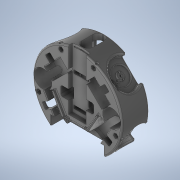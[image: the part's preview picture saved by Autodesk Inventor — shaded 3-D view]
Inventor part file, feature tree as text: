
AUTODESK INVENTOR PART (.ipt)
format: ipt  version: 2020.4 (Build 244396000, 396)  size: 3,471,872 bytes
history: native  units: mm
features: extrude x76, sketch x74, projected_geometry x35, fillet x19, other x9, chamfer x4, plane x2, mirror x1
ambient origin geometry x8: Origin, YZ Plane, XZ Plane, XY Plane, X Axis, Y Axis, Z Axis, Center Point
bodies: Solid1 (feature_tree)
feature tree (220):
  extrude  "Cilinder"  Depth=54.0mm TaperAngle=0.0deg
  other  "Motor Axis"
  other  "Plano M1"
  other  "Plano M2"
  other  "Plano M3"
  other  "Plano M4"
  extrude  "Roda M1"  Depth=176.0mm
  extrude  "Roda M2"  TaperAngle=60.0deg  [1 undecoded]
  extrude  "Roda M3"  TaperAngle=45.0deg  [1 undecoded]
  extrude  "Roda M4"  TaperAngle=0.0deg  [1 undecoded]
  extrude  "MotorsFitting"  Depth=14.6mm TaperAngle=0.0deg
  fillet  "MotorsCurve"  Radius=55.0mm
  extrude  "Threads M1"  Depth=20.0mm
  extrude  "Threads M2"  Depth=55.0mm
  extrude  "Threads M3"  Depth=20.0mm
  extrude  "Threads M4"  Depth=55.0mm
  extrude  "Threads Head M1"  Depth=20.0mm
  extrude  "Threads Head M2"  Depth=9.4mm
  extrude  "Threads Head M3"  Depth=9.4mm
  extrude  "Threads Head M4"  Depth=23.0mm
  extrude  "Thread Depth M1"  Depth=9.4mm
  extrude  "Thread Depth M2"  Depth=45.0mm
  extrude  "Thread Depth M3"  Depth=45.0mm
  extrude  "Thread Depth M4"  Depth=30.0mm
  extrude  "Threads Nut Head M1"  Depth=32.5mm
  extrude  "Threads Nut Head M2"  Depth=40.0mm TaperAngle=0.0deg
  extrude  "Threads Nut Head M3"  Depth=5.0mm
  extrude  "Threads Nut Head M4"  TaperAngle=0.0deg  [1 undecoded]
  extrude  "Wheel Fitting M1"  Depth=3.0mm
  extrude  "Wheel Fitting M2"  TaperAngle=0.0deg  [1 undecoded]
  extrude  "Wheel Fitting M3"  Depth=30.0mm TaperAngle=360.0deg
  extrude  "Wheel Fitting M4"  Depth=2.0mm
  extrude  "Capacitors"  Depth=6.0mm
  extrude  "Gear Entrance M1"  Depth=19.5mm
  extrude  "Gear Entrance M2"  Depth=10.0mm
  extrude  "Gear Entrance M3"  Depth=2.0mm
  extrude  "Gear Entrance M4"  Depth=2.0mm
  fillet  "Rounding Edges"  Radius=3.0mm
  fillet  "Rounding Motor Entrances"  Radius=6.0mm
  extrude  "Standoff Fitting"  TaperAngle=0.0deg  [1 undecoded]
  extrude  "Standoff Thread M1"  Depth=19.6mm
  extrude  "Standoff Thread M2"  Depth=19.5mm
  extrude  "Standoff Thread M3"  TaperAngle=0.0deg  [1 undecoded]
  extrude  "Standoff Thread M4"  Depth=30.0mm TaperAngle=360.0deg
  other  "Standoff Plane M1"
  other  "Standoff Plane M2"
  other  "Standoff Plane M3"
  other  "Standoff Plane M4"
  extrude  "Standoff Head M1"  Depth=10.0mm
  extrude  "Standoff Head M2"  Depth=2.0mm
  extrude  "Standoff Head M3"  TaperAngle=0.0deg  [1 undecoded]
  extrude  "Standoff Head M4"  Depth=6.0mm
  extrude  "Dribbler Entrance"  Depth=19.5mm
  extrude  "Battery Fitting"  Depth=19.6mm
  fillet  "Motor to Battery Edges"  Radius=3.0mm
  extrude  "Front Kicker"  Depth=11.0mm
  fillet  "Front Edges"  Radius=30.0mm
  extrude  "Cover Inlet"  Depth=10.0mm TaperAngle=0.0deg
  extrude  "Capacitors Holes"  Depth=2.0mm
  extrude  "Dribbler Motor Space"  Depth=2.0mm
  extrude  "IR Holder"  TaperAngle=0.0deg  [1 undecoded]
  fillet  "Dribbler and Kicker Edges"  Radius=19.5mm
  fillet  "Minor Fixes"  Radius=19.5mm
  chamfer  "Dribbler Chanfer"  Distance=30.0mm Angle=360.0deg
  extrude  "Capacitor Cable Fittng 1"  Depth=10.0mm TaperAngle=0.0deg
  fillet  "Capacitor Cable Rounding"  Radius=5.5mm
  extrude  "Special Nut M1"  Depth=5.5mm
  extrude  "Special Nut M2"  Depth=5.5mm
  extrude  "Special Nut M3"  Depth=5.5mm
  extrude  "Special Nut M4"  Depth=5.5mm
  extrude  "Special Nut Cylinder M1"  Depth=5.5mm
  extrude  "Special Nut Cylinder M2"  Depth=5.5mm
  extrude  "Special Nut Cylinder M3"  Depth=5.5mm
  extrude  "Special Nut Cylinder M4"  Depth=4.0mm
  fillet  "Special Nut Rounding"  Radius=4.0mm
  extrude  "Kicker Plate Fit 1"  Depth=4.0mm
  extrude  "Kicker Front Opening"  Depth=17.75mm TaperAngle=0.0deg
  extrude  "Kicker Base Fit"  Depth=4.0mm
  extrude  "Coil and Plinge Fitting"  Depth=4.0mm
  extrude  "Kicker Pkate Plunge Fit"  Depth=17.75mm TaperAngle=0.0deg
  chamfer  "Plunge Entrance 1"  Distance=17.6mm
  chamfer  "Plunge Entrance 2"  Distance=17.6mm
  fillet  "Fillet11"  Radius=15.5mm
  chamfer  "Coil Edges 1"  Distance=17.6mm
  extrude  "Kicker Plate Threads"  Depth=32.0mm
  extrude  "kicker Plate Nut 1"  Depth=2.0mm
  extrude  "Kicker Plate Nut 2"  Depth=2.0mm
  extrude  "Kicker Plunge Fit"  Depth=2.0mm
  fillet  "Kicker Plunge Round"  Radius=68.0mm
  fillet  "Wheel Round"  Radius=50.0mm
  extrude  "Capacitor Cables"  Depth=2.0mm
  fillet  "Capacitor Cable Round 1"  Radius=14.0mm
  fillet  "Capacitor Cable Round 2"  Radius=10.0mm
  extrude  "MotorProtection"  Depth=2.0mm
  fillet  "Motor Protection Round"  Radius=10.0mm
  extrude  "Extrusion86"  Depth=2.0mm TaperAngle=0.0deg
  extrude  "Extrusion87"  Depth=2.0mm
  fillet  "Fillet17"  Radius=10.0mm
  extrude  "Extrusion88"  Depth=2.0mm TaperAngle=0.0deg
  plane  "Work Plane14"
  extrude  "Extrusion89"  Depth=2.0mm
  extrude  "Extrusion91"  Depth=10.0mm
  mirror  "Mirror3"
  fillet  "Fillet18"  Radius=14.0mm
  extrude  "Extrusion92"  Depth=2.0mm
  fillet  "Fillet19"  Radius=2.0mm
  extrude  "Extrusion93"  Depth=2.0mm
  fillet  "Fillet20"  Radius=22.0mm
  extrude  "Extrusion94"  Depth=2.0mm
  extrude  "Extrusion95"  Depth=2.0mm
  sketch  "Sketch1"  dims[d0=176.0mm d1=54.0mm d2=0.0mm]
  sketch  "Sketch3"  dims[d3=180.0mm d4=176.0mm]
  sketch  "Sketch4"  dims[d5=60.0deg d6=60.0deg]
  sketch  "Sketch5"  dims[d8=45.0deg d9=45.0deg]
  sketch  "Sketch6"  dims[d10=55.0mm d11=0.0mm]
  sketch  "Sketch7"  dims[d12=20.0mm d13=14.6mm d14=0.0mm d15=55.0mm]
  sketch  "Sketch8"  dims[d16=0.0mm d17=20.0mm]
  sketch  "Sketch9"  dims[d18=14.6mm d19=0.0mm d20=55.0mm]
  sketch  "Sketch10"  dims[d21=0.0mm d22=20.0mm]
  sketch  "Sketch11"  dims[d23=14.6mm d24=0.0mm d25=55.0mm]
  sketch  "Sketch12"  dims[d26=0.0mm d27=20.0mm]
  sketch  "Sketch13"  dims[d28=14.6mm d29=0.0mm d30=9.4mm]
  sketch  "Sketch14"  dims[d32=9.4mm d33=9.4mm]
  sketch  "Sketch15"  dims[d34=23.0mm d35=23.0mm]
  sketch  "Sketch16"  dims[d37=23.0mm d38=9.4mm]
  sketch  "Sketch17"  dims[d39=23.0mm d40=45.0mm]
  sketch  "Sketch18"  dims[d41=45.0mm d42=45.0mm]
  sketch  "Sketch19"  dims[d43=45.0mm d44=30.0mm]
  sketch  "Sketch20"  dims[d45=30.0mm d46=32.5mm]
  sketch  "Sketch21"  dims[d47=32.5mm d48=40.0mm d49=0.0mm]
  sketch  "Sketch22"  dims[d50=22.5mm d51=5.0mm]
  sketch  "Sketch23"  dims[d52=12.5mm d53=0.0mm]
  sketch  "Sketch24"  dims[d54=19.5mm d55=3.0mm]
  sketch  "Sketch25"  dims[d56=19.6mm d58=0.0mm]
  sketch  "Sketch26"  dims[d59=11.0mm d60=30.0mm d62=360.0deg]
  sketch  "Sketch27"  dims[d64=2.0mm d65=2.0mm]
  sketch  "Sketch28"  dims[d66=6.0mm d67=6.0mm]
  sketch  "Sketch29"  dims[d68=19.5mm d69=19.5mm]
  sketch  "Sketch30"  dims[d70=10.0mm d71=0.0mm d72=2.5mm]
  projected_geometry  "Projected Loop1"
  sketch  "Sketch31"  dims[d73=5.0mm d74=2.0mm]
  projected_geometry  "Projected Loop2"
  sketch  "Sketch32"  dims[d75=2.0mm d76=12.5mm d77=3.0mm d78=6.0mm]
  projected_geometry  "Projected Loop3"
  sketch  "Sketch33"  dims[d79=6.0mm d80=0.0mm]
  projected_geometry  "Projected Loop4"
  sketch  "Sketch34"  dims[d81=19.5mm d82=19.6mm]
  sketch  "Sketch35"  dims[d83=19.5mm d84=19.5mm]
  projected_geometry  "Projected Loop5"
  sketch  "Sketch36"  dims[d85=5.0mm d86=0.0mm]
  projected_geometry  "Projected Loop6"
  sketch  "Sketch37"  dims[d87=11.0mm d88=30.0mm d90=360.0deg]
  projected_geometry  "Projected Loop7"
  sketch  "Sketch38"  dims[d92=10.0mm d93=0.0mm d94=5.0mm]
  projected_geometry  "Projected Loop8"
  sketch  "Sketch39"  dims[d95=12.5mm d96=2.0mm]
  sketch  "Sketch40"  dims[d97=2.0mm d98=0.0mm]
  sketch  "Sketch41"  dims[d99=19.5mm d100=6.0mm]
  sketch  "Sketch42"  dims[d101=6.0mm d102=19.5mm]
  sketch  "Sketch43"  dims[d103=19.5mm d104=19.6mm d105=3.0mm]
  sketch  "Sketch44"  dims[d106=0.0mm d107=11.0mm d108=30.0mm d110=360.0deg]
  projected_geometry  "Projected Loop9"
  projected_geometry  "Projected Loop10"
  sketch  "Sketch45"  dims[d112=5.0mm d113=10.0mm d114=0.0mm]
  sketch  "Sketch46"  dims[d115=5.0mm d116=2.0mm]
  projected_geometry  "Projected Loop11"
  projected_geometry  "Projected Loop12"
  sketch  "Sketch48"  dims[d117=2.0mm d118=6.0mm]
  projected_geometry  "Projected Loop14"
  sketch  "Sketch50"  dims[d119=6.0mm d120=0.0mm d121=19.5mm d122=19.5mm]
  projected_geometry  "Projected Loop15"
  sketch  "Sketch59"  dims[d123=19.5mm]
  sketch  "Sketch64"  dims[d124=12.5mm]
  sketch  "Sketch65"  dims[d125=19.6mm]
  projected_geometry  "Projected Loop27"
  sketch  "Sketch66"  dims[d126=3.0mm]
  projected_geometry  "Projected Loop28"
  sketch  "Sketch67"  dims[d127=0.0mm]
  sketch  "Sketch68"  dims[d128=11.0mm d129=30.0mm d131=360.0deg]
  sketch  "Sketch69"  dims[d133=2.5mm d134=10.0mm d135=0.0mm d136=5.5mm]
  sketch  "Sketch70"  dims[d137=5.5mm d138=5.5mm]
  sketch  "Sketch71"  dims[d139=18.0mm d140=0.0mm d141=5.5mm]
  sketch  "Sketch72"  dims[d142=5.5mm d143=5.5mm]
  projected_geometry  "Projected Loop29"
  sketch  "Sketch73"  dims[d144=18.0mm d145=0.0mm d146=5.5mm]
  sketch  "Sketch74"  dims[d147=5.5mm d148=5.5mm]
  projected_geometry  "Projected Loop30"
  sketch  "Sketch75"  dims[d149=18.0mm d150=0.0mm d151=5.5mm]
  projected_geometry  "Projected Loop31"
  sketch  "Sketch76"  dims[d152=5.5mm d153=5.5mm]
  projected_geometry  "Projected Loop32"
  projected_geometry  "Projected Loop33"
  sketch  "Sketch77"  dims[d154=18.0mm d155=0.0mm d156=4.0mm d157=4.0mm]
  projected_geometry  "Projected Loop34"
  projected_geometry  "Projected Loop35"
  projected_geometry  "Projected Loop36"
  projected_geometry  "Projected Loop37"
  sketch  "Sketch78"  dims[d158=17.75mm d159=0.0mm d160=4.0mm]
  sketch  "Sketch80"  dims[d161=4.0mm d162=17.75mm d163=0.0mm]
  projected_geometry  "Projected Loop38"
  projected_geometry  "Projected Loop39"
  projected_geometry  "Projected Loop40"
  projected_geometry  "Projected Loop41"
  sketch  "Sketch81"  dims[d164=4.0mm d165=4.0mm]
  sketch  "Sketch82"  dims[d166=17.75mm d167=0.0mm d168=4.0mm]
  sketch  "Sketch89"  dims[d169=4.0mm d170=17.75mm d171=0.0mm]
  sketch  "Sketch90"  dims[d172=15.5mm]
  sketch  "Sketch92"  dims[d173=32.0mm d174=17.6mm d175=0.0mm]
  sketch  "Sketch93"  dims[d176=15.5mm]
  sketch  "Sketch95"  dims[d177=32.0mm d178=17.6mm d179=0.0mm d180=15.5mm]
  plane  "Work Plane15"
  projected_geometry  "Projected Loop46"
  projected_geometry  "Projected Loop47"
  projected_geometry  "Projected Loop48"
  sketch  "Sketch97"  dims[d181=32.0mm d182=17.6mm d183=0.0mm]
  sketch  "Sketch98"  dims[d184=15.5mm d185=32.0mm]
  projected_geometry  "Projected Loop49"
  projected_geometry  "Projected Loop50"
  projected_geometry  "Projected Loop51"
  sketch  "Sketch99"  dims[d186=17.6mm d187=0.0mm d188=35.7mm d189=4.15mm d190=68.0mm d191=68.0mm d192=50.0mm d193=0.0mm d195=12.5mm d196=14.0mm d197=0.0mm d198=10.0mm d199=12.5mm d200=10.0mm d201=14.0mm d202=0.0mm d203=12.5mm d204=10.0mm d205=14.0mm d206=0.0mm d207=12.5mm d208=10.0mm d209=14.0mm d210=0.0mm d211=3.0mm d212=2.0mm d213=2.0mm d214=2.0mm d215=22.0mm d216=76.0mm d217=4.22mm d218=72.0mm d219=32.0mm d220=4.22mm d221=8.0mm d222=0.0mm d223=3.0mm d224=3.5mm d225=2.436418mm d226=24.0mm d227=0.0mm d228=3.0mm d229=3.5mm d230=2.436418mm d231=24.0mm d232=0.0mm d233=3.0mm d234=3.5mm d235=2.436418mm d236=24.0mm d237=0.0mm d238=3.0mm d239=3.5mm d240=2.436418mm d241=24.0mm d242=0.0mm d243=90.0mm d244=40.0mm d245=0.0mm d246=55.0mm d247=10.0mm d248=0.0mm d249=2.0mm d250=0.0mm d251=2.0mm d252=0.0mm d253=2.0mm d254=0.0mm d255=2.0mm d256=0.0mm d257=2.0mm d258=1.5mm d259=35.0mm d260=120.0mm d261=0.0mm d262=28.5mm d263=8.0mm d264=0.0mm d265=1.5mm d266=-2.0mm d267=-2.0mm d268=-2.0mm d269=-2.0mm d270=5.5mm d271=4.0mm d272=0.0mm d273=5.5mm d274=4.0mm d275=0.0mm d276=5.5mm d277=4.0mm d278=0.0mm d279=5.5mm d280=4.0mm d281=0.0mm d282=56.5mm d283=12.5mm d284=0.0mm d285=17.0mm d286=10.0mm d287=0.0mm d288=2.0mm d289=3.0mm d299=82.0mm d300=17.453293mm d301=3.490659mm d302=84.0mm d303=17.453293mm d304=3.490659mm d305=8.0mm d306=0.0mm d307=0.4mm d308=22.0mm d309=22.0mm d310=10.0mm d311=0.0mm d317=90.0mm d318=14.0mm d319=0.0mm d320=0.0mm d321=11.0mm d322=0.0mm d327=3.75mm d328=17.11mm d329=0.0mm d330=24.43461mm d331=7.1mm d332=0.0mm d355=2.0mm d356=2.0mm d357=45.0deg d358=3.0mm d359=2.0mm d396=5.5mm d397=10.0mm d398=23.0mm d399=16.0mm d400=56.0mm d401=0.0mm d402=5.5mm d403=0.0mm d404=1.5mm d429=8.1mm d430=16.1mm d431=6.0mm d432=3.0mm d433=0.0mm d434=0.0mm d435=16.1mm d436=8.1mm d437=6.0mm d438=3.0mm d439=0.0mm d440=0.0mm d441=16.1mm d442=8.1mm d443=6.0mm d444=3.0mm d445=0.0mm d446=0.0mm d447=8.1mm d448=16.1mm d449=6.0mm d450=3.0mm d451=0.0mm d452=0.0mm d453=8.1mm d454=5.75mm d455=0.0mm d456=8.1mm d457=5.75mm d458=0.0mm d459=8.1mm d460=5.75mm d461=0.0mm d462=8.1mm d463=5.75mm d464=0.0mm d465=0.9mm d466=29.2mm d467=135.0mm d468=0.0mm d469=14.6mm d470=76.25mm d471=43.2mm d472=7.1mm d473=0.0mm d474=43.2mm d475=7.1mm d476=0.0mm d477=34.5mm d478=79.5mm d479=6.0mm d480=0.0mm d481=30.9mm d482=41.0mm d483=0.0mm d485=29.2mm d486=6.2mm d490=46.1mm d491=0.0mm d492=29.2mm d493=6.2mm d494=3.6mm d495=3.6mm d496=44.8mm d497=0.0mm d498=7.0mm d499=0.0mm d500=6.4mm d501=3.6mm d502=45.0deg d503=6.4mm d504=3.6mm d505=45.0deg d507=10.0mm d508=7.5mm d509=4.6mm d510=60.0deg d511=3.0mm d512=3.0mm d513=18.0mm d514=18.0mm d515=3.0mm d516=3.0mm d517=18.0mm d518=18.0mm d519=3.55mm d520=3.55mm d521=3.55mm d522=3.55mm d523=12.0mm d524=0.0mm d525=5.6mm d526=2.4mm d527=5.6mm d528=2.4mm d529=3.0mm d530=3.0mm d531=1.3mm d532=1.3mm d533=39.8mm d534=0.0mm d535=60.0deg d536=60.0deg d537=120.0deg d538=120.0deg d539=60.0deg d540=60.0deg d541=120.0deg d542=120.0deg d543=10.0mm d544=0.0mm d545=22.0mm d546=20.0mm d547=11.0mm d548=12.5mm d549=10.0mm d550=0.0mm d551=10.0mm d552=3.0mm d553=2.0mm d554=3.0mm d555=18.0mm d556=19.0mm d557=18.0mm d558=19.0mm d559=23.6mm d560=23.6mm d561=7.5mm d562=7.5mm d563=47.0mm d564=0.0mm d565=2.0mm d566=2.0mm d567=4.0mm d568=5.0mm d609=0.0mm d611=5.0mm d612=0.0mm d613=3.75mm d614=0.0mm d616=0.0mm d617=5.0mm d618=3.75mm d619=6.0mm d620=0.0mm d621=1.75mm d622=0.75mm d623=5.5mm d624=9.5mm d625=9.25mm d626=25.9mm d627=8.5mm d628=0.0mm d632=3.0mm d633=0.0mm d636=7.4mm d637=0.0mm d638=3.0mm d639=3.0mm d640=4.0mm d641=3.75mm d642=131.25mm d643=0.0mm d644=-8.0mm d645=5.5mm d646=10.0mm d647=0.0mm d650=10.0mm d651=10.0mm d653=16.0mm d654=2.5mm d655=0.0mm d656=1.0mm d657=2.0mm d664=1.0mm d665=0.0mm d666=19.9mm d667=0.5mm d668=53.9mm d669=25.0mm d670=10.25mm d671=26.12407mm d672=8.0mm d673=90.0deg d674=90.0deg d675=90.0deg d676=90.0deg d677=90.0deg d678=90.0deg d679=90.0deg d680=4.0mm d681=2.0mm d682=29.2mm d683=10.0mm d684=0.0mm d685=2.0mm d686=0.5mm d687=3.0mm d688=3.0mm d689=6.5mm d691=6.5mm d692=4.0mm d693=10.0mm d694=0.0mm d695=5.5mm d696=5.5mm d697=2.0mm d698=2.1mm d699=0.0mm d700=0.0mm d701=4.0mm d702=0.0mm]
note: 9 required parameter values undecoded (feature->parameter linkage not recoverable at this tier; creation-order binding heuristic only, values carry confidence <= 0.55)
